# Revit family: Deca_Assento plástico com slow close_Flex_AP.385
name_source: partatom
category: Plumbing Fixtures
units: mm (PartAtom-declared; Revit-internal decimal feet)

## family parameters
Cut with Voids When Loaded = No
Host = Face
Part Type = Normal
Room Calculation Point = No
Round Connector Dimension = Use Diameter
Shared = No

## types (1)
- AP.385.17_Branco
    Acompanha o Produto = FIXAÇÃO ASSENTO
    Aprovado por = quattroD
    Atendimento ao Cliente = 0800-0117073
    Categoria = ASSENTOS
    Composição Anel Vedação = -
    Composição Assento = -
    Composição Básica = Plástico de Engenharia (PoliPropileno) (PP)
    Composição Componente = Não Possui
    Consumo = -
    Cor Interna = -
    Cor Principal = Branco
    Cor Secundária = -
    Cores Componente = -
    Criado por = quattroD
    Código Pai = AP.385
    Default Elevation = 0 m
    Description = Assento Plástico com slow close
    Informações Complementares = -
    Itens de Instalação = -
    Linha = Assento Plástico com Slow
    Manufacturer = Deca
    Material = Deca_Plástico - Branco
    Material Secundário = Deca_Ligas de Cobre (Bronze e Latão)
    Model = AP.385.17
    Norma = NBR-16729
    Peso Líquido (Kg) = 1.228
    Pressão máx. funcionamento = -
    Pressão mín. Aquec. Acúmulo = -
    Pressão mín. Aquec. Passagem = -
    Pressão mín. funcionamento = -
    Saída de Esgoto = -
    Segmento = Banheiro Competitivo
    Tipo de dispositivo economizador = -
    Tipo de mecanismo utilizado = -
    Tipo de rosca de entrada = -
    Tipo de rosca de saída = -
    URL = www.deca.com.br
    Vazão na Pressão máx. (L/min) = -
    Vazão na Pressão mín. (L/min) = -

## geometry (parser evidence)
native form markers: Sweep x2
no freeform markers — native parametric forms only
